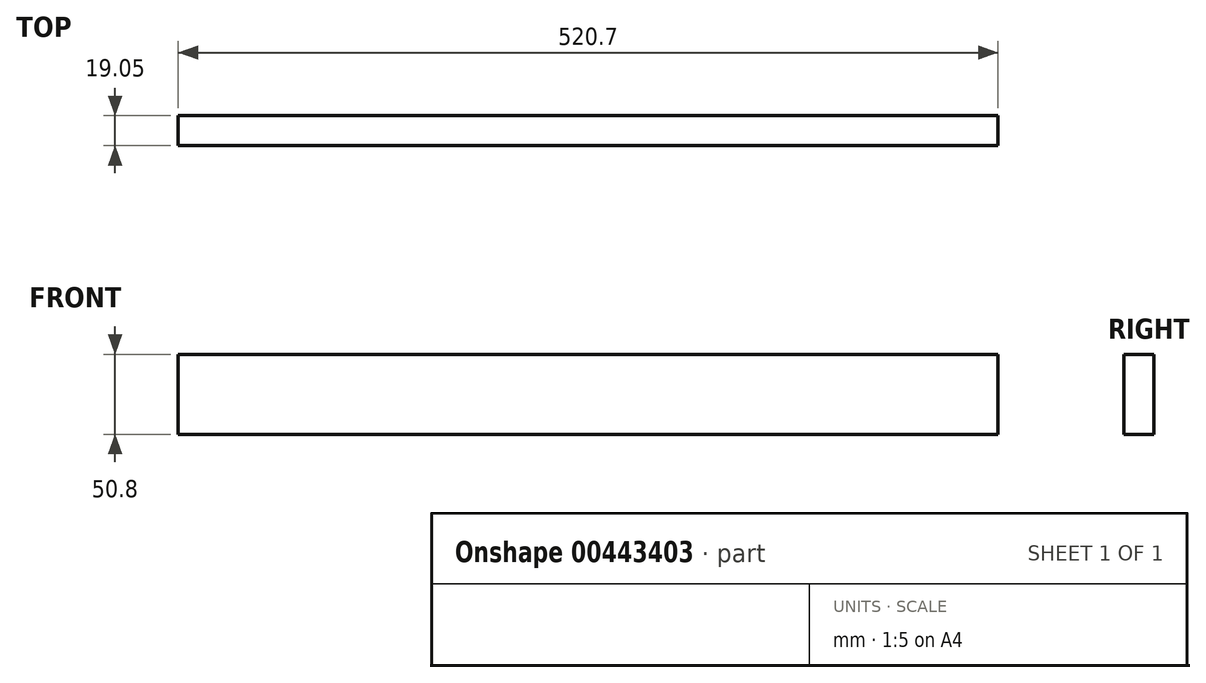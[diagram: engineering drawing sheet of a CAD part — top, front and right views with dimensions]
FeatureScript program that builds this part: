
annotation { "Feature Type Name" : "Feature", "Feature Type Description" : "" }
export const myFeature = defineFeature(function(context is Context, id is Id, definition is map)
    precondition{}
    {
        {
            var Q0;
            Q0=qCreatedBy(makeId("Front.planeOp"),FACE);
            var sketch = newSketch(context, id + "F0", { "sketchPlane" : qUnion([Q0])});
            skLineSegment(sketch, "E0.bottom", {"start": v(260.35, -25.4) * mm, "end": v(-260.35, -25.4) * mm});
            skLineSegment(sketch, "E0.top", {"start": v(260.35, 25.4) * mm, "end": v(-260.35, 25.4) * mm});
            skLineSegment(sketch, "E0.left", {"start": v(260.35, -25.4) * mm, "end": v(260.35, 25.4) * mm});
            skLineSegment(sketch, "E0.right", {"start": v(-260.35, -25.4) * mm, "end": v(-260.35, 25.4) * mm});
            skPoint(sketch, "E0.middle", {"position": v(0, 0) * mm});
            skSolve(sketch);
        }
        {
            var Q0;
            Q0=qSketchRegion(id+"F0",true);
            extrude(context, id + "F1", {"entities" : qUnion([Q0]), "depth" : 19.05 * mm});
        }
    });
